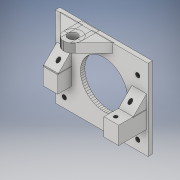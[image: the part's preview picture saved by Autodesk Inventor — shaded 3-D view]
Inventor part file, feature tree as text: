
AUTODESK INVENTOR PART (.ipt)
format: ipt  version: 2017 (Build 210142000, 142)  size: 796,672 bytes
history: native  units: in
note: dims shown in document units (in); Inventor stores cm internally (conversion verified against a paired STEP export)
features: projected_geometry x2, extrude x1, sketch x1, imported_body x1
ambient origin geometry x8: Origin, YZ Plane, XZ Plane, XY Plane, X Axis, Y Axis, Z Axis, Center Point
bodies: Solid1 (feature_tree)
feature tree (5):
  extrude  "Extrusion1"  Depth=0.3937in TaperAngle=0.0deg
  sketch  "Sketch1"  dims[d0=0.252in d1=0.3937in d2=0.0in]
  projected_geometry  "Projected Loop1"
  projected_geometry  "Projected Loop2"
  imported_body  "Base1"
